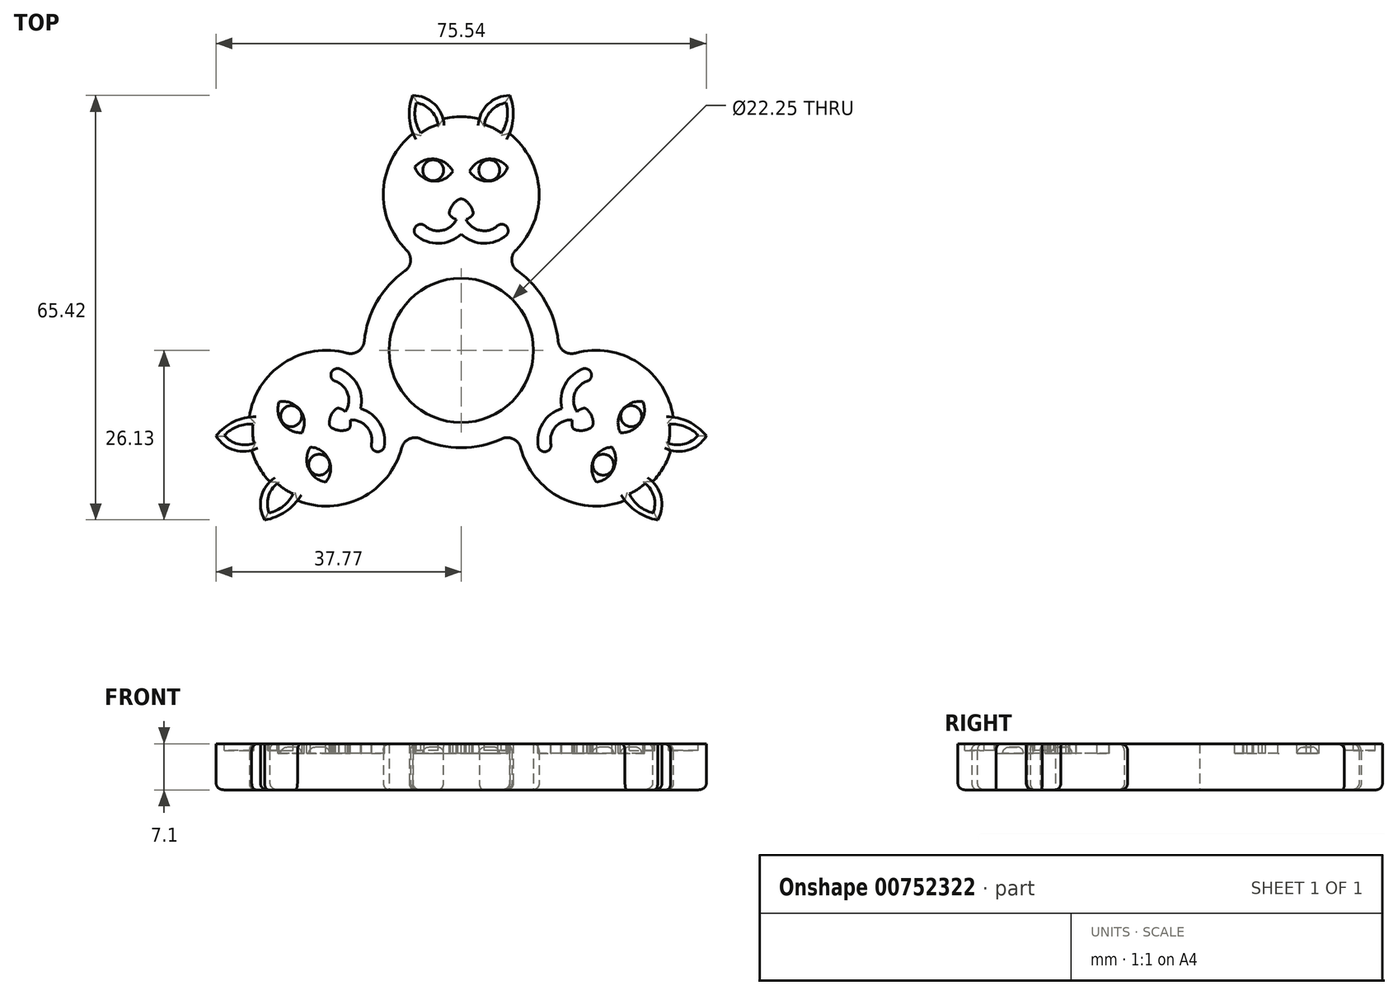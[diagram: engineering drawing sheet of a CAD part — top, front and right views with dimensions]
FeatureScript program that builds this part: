
annotation { "Feature Type Name" : "Feature", "Feature Type Description" : "" }
export const myFeature = defineFeature(function(context is Context, id is Id, definition is map)
    precondition{}
    {
        {
            var Q0;
            Q0=qCreatedBy(makeId("Top.planeOp"),FACE);
            var sketch = newSketch(context, id + "F0", { "sketchPlane" : qUnion([Q0])});
            skCircle(sketch, "E0", {"center": v(0, 0) * mm, "radius": 11.13 * mm});
            skCircle(sketch, "E1", {"center": v(0, 0) * mm, "radius": 15 * mm});
            skSolve(sketch);
        }
        {
            var Q0;
            Q0 = qSketchRegion(id + "F0", true);
            extrude(context, id + "F1", {"entities" : qUnion([Q0]), "depth" : 7.1 * mm, "offsetDistance" : 25 * mm});
        }
        {
            var Q0;
            Q0=qCreatedBy(makeId("Top.planeOp"),FACE);
            var sketch = newSketch(context, id + "F2", { "sketchPlane" : qUnion([Q0])});
            skArc(sketch, "E2", {"start": v(-7.5, 39.3) * mm, "mid": v(-8.02, 36.35) * mm, "end": v(-7.42, 33.43) * mm});
            skArc(sketch, "E3", {"start": v(-2.8, 35.67) * mm, "mid": v(-4.52, 38.28) * mm, "end": v(-7.5, 39.3) * mm});
            skArc(sketch, "E4", {"start": v(-8.69, 12.23) * mm, "mid": v(-7.8, 13.78) * mm, "end": v(-8.43, 15.46) * mm});
            skArc(sketch, "E5.MirrorCS", {"start": v(2.8, 35.67) * mm, "mid": v(4.52, 38.28) * mm, "end": v(7.5, 39.3) * mm});
            skArc(sketch, "E6.MirrorCS", {"start": v(7.5, 39.3) * mm, "mid": v(8.02, 36.35) * mm, "end": v(7.42, 33.43) * mm});
            skArc(sketch, "E7.MirrorCS", {"start": v(8.69, 12.23) * mm, "mid": v(7.8, 13.78) * mm, "end": v(8.43, 15.46) * mm});
            skArc(sketch, "E8", {"start": v(8.43, 15.46) * mm, "mid": v(11.98, 24.67) * mm, "end": v(7.42, 33.43) * mm});
            skArc(sketch, "E9", {"start": v(8.69, 12.23) * mm, "mid": v(0, 15) * mm, "end": v(-8.69, 12.23) * mm});
            skArc(sketch, "E10", {"start": v(2.8, 35.67) * mm, "mid": v(0, 36) * mm, "end": v(-2.8, 35.67) * mm});
            skArc(sketch, "E11", {"start": v(-7.42, 33.43) * mm, "mid": v(-11.98, 24.67) * mm, "end": v(-8.43, 15.46) * mm});
            skArc(sketch, "E12.1.0", {"start": v(-30.28, -26.13) * mm, "mid": v(-27.48, -25.12) * mm, "end": v(-25.24, -23.14) * mm});
            skArc(sketch, "E12.1.1", {"start": v(-32.29, -15.42) * mm, "mid": v(-35.42, -15.22) * mm, "end": v(-37.77, -13.16) * mm});
            skArc(sketch, "E12.1.2", {"start": v(-29.5, -20.25) * mm, "mid": v(-30.9, -23.06) * mm, "end": v(-30.28, -26.13) * mm});
            skArc(sketch, "E12.1.3", {"start": v(-17.6, -0.43) * mm, "mid": v(-27.35, -1.96) * mm, "end": v(-32.66, -10.28) * mm});
            skArc(sketch, "E12.1.4", {"start": v(-14.93, 1.4) * mm, "mid": v(-13, -7.5) * mm, "end": v(-6.25, -13.64) * mm});
            skArc(sketch, "E12.1.5", {"start": v(-37.77, -13.16) * mm, "mid": v(-35.5, -11.23) * mm, "end": v(-32.66, -10.28) * mm});
            skArc(sketch, "E12.1.6", {"start": v(-25.24, -23.14) * mm, "mid": v(-15.37, -22.71) * mm, "end": v(-9.17, -15.03) * mm});
            skArc(sketch, "E12.1.7", {"start": v(-32.29, -15.42) * mm, "mid": v(-31.18, -18) * mm, "end": v(-29.5, -20.25) * mm});
            skArc(sketch, "E12.1.8", {"start": v(-6.25, -13.64) * mm, "mid": v(-8.03, -13.65) * mm, "end": v(-9.17, -15.03) * mm});
            skArc(sketch, "E12.1.9", {"start": v(-14.93, 1.4) * mm, "mid": v(-15.84, -0.13) * mm, "end": v(-17.6, -0.43) * mm});
            skArc(sketch, "E12.2.0", {"start": v(37.77, -13.16) * mm, "mid": v(35.5, -11.23) * mm, "end": v(32.66, -10.28) * mm});
            skArc(sketch, "E12.2.1", {"start": v(29.5, -20.25) * mm, "mid": v(30.9, -23.06) * mm, "end": v(30.28, -26.13) * mm});
            skArc(sketch, "E12.2.2", {"start": v(32.29, -15.42) * mm, "mid": v(35.42, -15.22) * mm, "end": v(37.77, -13.16) * mm});
            skArc(sketch, "E12.2.3", {"start": v(9.17, -15.03) * mm, "mid": v(15.37, -22.71) * mm, "end": v(25.24, -23.14) * mm});
            skArc(sketch, "E12.2.4", {"start": v(6.25, -13.64) * mm, "mid": v(13, -7.5) * mm, "end": v(14.93, 1.4) * mm});
            skArc(sketch, "E12.2.5", {"start": v(30.28, -26.13) * mm, "mid": v(27.48, -25.12) * mm, "end": v(25.24, -23.14) * mm});
            skArc(sketch, "E12.2.6", {"start": v(32.66, -10.28) * mm, "mid": v(27.35, -1.96) * mm, "end": v(17.6, -0.43) * mm});
            skArc(sketch, "E12.2.7", {"start": v(29.5, -20.25) * mm, "mid": v(31.18, -18) * mm, "end": v(32.29, -15.42) * mm});
            skArc(sketch, "E12.2.8", {"start": v(14.93, 1.4) * mm, "mid": v(15.84, -0.13) * mm, "end": v(17.6, -0.43) * mm});
            skArc(sketch, "E12.2.9", {"start": v(6.25, -13.64) * mm, "mid": v(8.03, -13.65) * mm, "end": v(9.17, -15.03) * mm});
            skSolve(sketch);
        }
        {
            var Q0;
            Q0 = qSketchRegion(id + "F2", true);
            extrude(context, id + "F3", {"entities" : qUnion([Q0]), "operationType" : NewBodyOperationType.ADD, "depth" : 7.1 * mm, "offsetDistance" : 25 * mm});
        }
        {
            var Q0;
            Q0=makeQuery(id+"F3.boolean.opBoolean","MERGE",FACE,{"derivedFrom":[makeQuery(id+"F1.opExtrude","CAP_FACE",FACE,{"disambiguationData":[OSD([sQuery(id+"F0.wireOp",EDGE,"E0"),sQuery(id+"F0.wireOp",EDGE,"E1")])],"isStart":false}),makeQuery(id+"F3.opExtrude","CAP_FACE",FACE,{"disambiguationData":[OSD([sQuery(id+"F2.wireOp",EDGE,"E2"),sQuery(id+"F2.wireOp",EDGE,"E3"),sQuery(id+"F2.wireOp",EDGE,"E4"),sQuery(id+"F2.wireOp",EDGE,"E5.MirrorCS"),sQuery(id+"F2.wireOp",EDGE,"E6.MirrorCS"),sQuery(id+"F2.wireOp",EDGE,"E7.MirrorCS"),sQuery(id+"F2.wireOp",EDGE,"E8"),sQuery(id+"F2.wireOp",EDGE,"E9"),sQuery(id+"F2.wireOp",EDGE,"E10"),sQuery(id+"F2.wireOp",EDGE,"E11")])],"isStart":false}),makeQuery(id+"F3.opExtrude","CAP_FACE",FACE,{"disambiguationData":[OSD([sQuery(id+"F2.wireOp",EDGE,"E12.1.0"),sQuery(id+"F2.wireOp",EDGE,"E12.1.1"),sQuery(id+"F2.wireOp",EDGE,"E12.1.2"),sQuery(id+"F2.wireOp",EDGE,"E12.1.3"),sQuery(id+"F2.wireOp",EDGE,"E12.1.4"),sQuery(id+"F2.wireOp",EDGE,"E12.1.5"),sQuery(id+"F2.wireOp",EDGE,"E12.1.6"),sQuery(id+"F2.wireOp",EDGE,"E12.1.7"),sQuery(id+"F2.wireOp",EDGE,"E12.1.8"),sQuery(id+"F2.wireOp",EDGE,"E12.1.9")])],"isStart":false}),makeQuery(id+"F3.opExtrude","CAP_FACE",FACE,{"disambiguationData":[OSD([sQuery(id+"F2.wireOp",EDGE,"E12.2.0"),sQuery(id+"F2.wireOp",EDGE,"E12.2.1"),sQuery(id+"F2.wireOp",EDGE,"E12.2.2"),sQuery(id+"F2.wireOp",EDGE,"E12.2.3"),sQuery(id+"F2.wireOp",EDGE,"E12.2.4"),sQuery(id+"F2.wireOp",EDGE,"E12.2.5"),sQuery(id+"F2.wireOp",EDGE,"E12.2.6"),sQuery(id+"F2.wireOp",EDGE,"E12.2.7"),sQuery(id+"F2.wireOp",EDGE,"E12.2.8"),sQuery(id+"F2.wireOp",EDGE,"E12.2.9")])],"isStart":false})]});
            var sketch = newSketch(context, id + "F4", { "sketchPlane" : qUnion([Q0])});
            skArc(sketch, "E13", {"start": v(-1.28, 27.6) * mm, "mid": v(-4.05, 29.48) * mm, "end": v(-7.16, 28.24) * mm});
            skArc(sketch, "E14", {"start": v(-7.16, 28.24) * mm, "mid": v(-4.42, 26.1) * mm, "end": v(-1.28, 27.6) * mm});
            skArc(sketch, "E15", {"start": v(0, 23.34) * mm, "mid": v(-0.27, 23.3) * mm, "end": v(-0.5, 23.19) * mm});
            skArc(sketch, "E16", {"start": v(-0.5, 23.19) * mm, "mid": v(-1.36, 22.37) * mm, "end": v(-1.83, 21.28) * mm});
            skArc(sketch, "E17", {"start": v(-1.67, 20.75) * mm, "mid": v(-1.24, 20.41) * mm, "end": v(-0.74, 20.18) * mm});
            skArc(sketch, "E18", {"start": v(-1.83, 21.28) * mm, "mid": v(-1.81, 21) * mm, "end": v(-1.67, 20.75) * mm});
            skArc(sketch, "E19.MirrorCS", {"start": v(0, 23.34) * mm, "mid": v(0.27, 23.3) * mm, "end": v(0.5, 23.19) * mm});
            skArc(sketch, "E20.MirrorCS", {"start": v(0.5, 23.19) * mm, "mid": v(1.36, 22.37) * mm, "end": v(1.83, 21.28) * mm});
            skArc(sketch, "E21.MirrorCS", {"start": v(1.83, 21.28) * mm, "mid": v(1.81, 21) * mm, "end": v(1.67, 20.75) * mm});
            skArc(sketch, "E22.MirrorCS", {"start": v(1.67, 20.75) * mm, "mid": v(1.24, 20.41) * mm, "end": v(0.74, 20.18) * mm});
            skArc(sketch, "E23", {"start": v(-5.68, 19.27) * mm, "mid": v(-2.98, 18.47) * mm, "end": v(-0.74, 20.18) * mm});
            skArc(sketch, "E24", {"start": v(-7, 17.76) * mm, "mid": v(-3.47, 16.5) * mm, "end": v(0, 17.9) * mm});
            skArc(sketch, "E25", {"start": v(-5.68, 19.27) * mm, "mid": v(-7, 19.1) * mm, "end": v(-7, 17.76) * mm});
            skArc(sketch, "E26.MirrorCS", {"start": v(5.68, 19.27) * mm, "mid": v(2.98, 18.47) * mm, "end": v(0.74, 20.18) * mm});
            skArc(sketch, "E27.MirrorCS", {"start": v(5.68, 19.27) * mm, "mid": v(7, 19.1) * mm, "end": v(7, 17.76) * mm});
            skArc(sketch, "E28.MirrorCS", {"start": v(7, 17.76) * mm, "mid": v(3.47, 16.5) * mm, "end": v(0, 17.9) * mm});
            skArc(sketch, "E29.MirrorCS", {"start": v(7.16, 28.24) * mm, "mid": v(4.42, 26.1) * mm, "end": v(1.28, 27.6) * mm});
            skArc(sketch, "E30.MirrorCS", {"start": v(1.28, 27.6) * mm, "mid": v(4.05, 29.48) * mm, "end": v(7.16, 28.24) * mm});
            skLineSegment(sketch, "E31", {"start": v(0, 20.06) * mm, "end": v(0, 20.06) * mm});
            skArc(sketch, "E32.1.0", {"start": v(-24.54, -12.68) * mm, "mid": v(-27.55, -11.23) * mm, "end": v(-28.04, -7.92) * mm});
            skArc(sketch, "E32.1.1", {"start": v(-19.53, -4.72) * mm, "mid": v(-17.49, -6.66) * mm, "end": v(-17.85, -9.45) * mm});
            skArc(sketch, "E32.1.2", {"start": v(-18.88, -2.83) * mm, "mid": v(-16.02, -5.24) * mm, "end": v(-15.5, -8.95) * mm});
            skArc(sketch, "E32.1.3", {"start": v(-28.04, -7.92) * mm, "mid": v(-24.8, -9.22) * mm, "end": v(-24.54, -12.68) * mm});
            skArc(sketch, "E32.1.4", {"start": v(-23.25, -14.9) * mm, "mid": v(-23.5, -18.25) * mm, "end": v(-20.88, -20.32) * mm});
            skArc(sketch, "E32.1.5", {"start": v(-13.85, -14.55) * mm, "mid": v(-13.04, -15.6) * mm, "end": v(-11.89, -14.94) * mm});
            skArc(sketch, "E32.1.6", {"start": v(-20.88, -20.32) * mm, "mid": v(-20.38, -16.88) * mm, "end": v(-23.25, -14.9) * mm});
            skArc(sketch, "E32.1.7", {"start": v(-11.89, -14.94) * mm, "mid": v(-12.55, -11.25) * mm, "end": v(-15.5, -8.95) * mm});
            skArc(sketch, "E32.1.8", {"start": v(-13.85, -14.55) * mm, "mid": v(-14.5, -11.82) * mm, "end": v(-17.1, -10.73) * mm});
            skArc(sketch, "E32.1.9", {"start": v(-19.53, -4.72) * mm, "mid": v(-20.03, -3.49) * mm, "end": v(-18.88, -2.83) * mm});
            skArc(sketch, "E32.1.10", {"start": v(-19.35, -9.06) * mm, "mid": v(-19.1, -8.93) * mm, "end": v(-18.8, -8.93) * mm});
            skArc(sketch, "E32.1.11", {"start": v(-18.8, -8.93) * mm, "mid": v(-18.3, -9.13) * mm, "end": v(-17.85, -9.45) * mm});
            skArc(sketch, "E32.1.12", {"start": v(-20.21, -11.67) * mm, "mid": v(-20.05, -11.88) * mm, "end": v(-19.83, -12.03) * mm});
            skArc(sketch, "E32.1.13", {"start": v(-19.83, -12.03) * mm, "mid": v(-18.7, -12.36) * mm, "end": v(-17.52, -12.22) * mm});
            skArc(sketch, "E32.1.14", {"start": v(-20.33, -11.15) * mm, "mid": v(-20.05, -10) * mm, "end": v(-19.35, -9.06) * mm});
            skArc(sketch, "E32.1.15", {"start": v(-17.14, -11.82) * mm, "mid": v(-17.06, -11.28) * mm, "end": v(-17.1, -10.73) * mm});
            skArc(sketch, "E32.1.16", {"start": v(-17.52, -12.22) * mm, "mid": v(-17.28, -12.07) * mm, "end": v(-17.14, -11.82) * mm});
            skArc(sketch, "E32.1.17", {"start": v(-20.21, -11.67) * mm, "mid": v(-20.31, -11.42) * mm, "end": v(-20.33, -11.15) * mm});
            skArc(sketch, "E32.2.0", {"start": v(23.25, -14.9) * mm, "mid": v(23.5, -18.25) * mm, "end": v(20.88, -20.32) * mm});
            skArc(sketch, "E32.2.1", {"start": v(13.85, -14.55) * mm, "mid": v(14.5, -11.82) * mm, "end": v(17.1, -10.73) * mm});
            skArc(sketch, "E32.2.2", {"start": v(11.89, -14.94) * mm, "mid": v(12.55, -11.25) * mm, "end": v(15.5, -8.95) * mm});
            skArc(sketch, "E32.2.3", {"start": v(20.88, -20.32) * mm, "mid": v(20.38, -16.88) * mm, "end": v(23.25, -14.9) * mm});
            skArc(sketch, "E32.2.4", {"start": v(24.54, -12.68) * mm, "mid": v(27.55, -11.23) * mm, "end": v(28.04, -7.92) * mm});
            skArc(sketch, "E32.2.5", {"start": v(19.53, -4.72) * mm, "mid": v(20.03, -3.49) * mm, "end": v(18.88, -2.83) * mm});
            skArc(sketch, "E32.2.6", {"start": v(28.04, -7.92) * mm, "mid": v(24.8, -9.22) * mm, "end": v(24.54, -12.68) * mm});
            skArc(sketch, "E32.2.7", {"start": v(18.88, -2.83) * mm, "mid": v(16.02, -5.24) * mm, "end": v(15.5, -8.95) * mm});
            skArc(sketch, "E32.2.8", {"start": v(19.53, -4.72) * mm, "mid": v(17.49, -6.66) * mm, "end": v(17.85, -9.45) * mm});
            skArc(sketch, "E32.2.9", {"start": v(13.85, -14.55) * mm, "mid": v(13.04, -15.6) * mm, "end": v(11.89, -14.94) * mm});
            skArc(sketch, "E32.2.10", {"start": v(17.52, -12.22) * mm, "mid": v(17.28, -12.07) * mm, "end": v(17.14, -11.82) * mm});
            skArc(sketch, "E32.2.11", {"start": v(17.14, -11.82) * mm, "mid": v(17.06, -11.28) * mm, "end": v(17.1, -10.73) * mm});
            skArc(sketch, "E32.2.12", {"start": v(20.21, -11.67) * mm, "mid": v(20.31, -11.42) * mm, "end": v(20.33, -11.15) * mm});
            skArc(sketch, "E32.2.13", {"start": v(20.33, -11.15) * mm, "mid": v(20.05, -10) * mm, "end": v(19.35, -9.06) * mm});
            skArc(sketch, "E32.2.14", {"start": v(19.83, -12.03) * mm, "mid": v(18.7, -12.36) * mm, "end": v(17.52, -12.22) * mm});
            skArc(sketch, "E32.2.15", {"start": v(18.8, -8.93) * mm, "mid": v(18.3, -9.13) * mm, "end": v(17.85, -9.45) * mm});
            skArc(sketch, "E32.2.16", {"start": v(19.35, -9.06) * mm, "mid": v(19.1, -8.93) * mm, "end": v(18.8, -8.93) * mm});
            skArc(sketch, "E32.2.17", {"start": v(20.21, -11.67) * mm, "mid": v(20.05, -11.88) * mm, "end": v(19.83, -12.03) * mm});
            skPoint(sketch, "E32.center", {"position": v(0, 0) * mm});
            skSolve(sketch);
        }
        {
            var Q0;
            Q0 = qSketchRegion(id + "F4", true);
            extrude(context, id + "F5", {"entities" : qUnion([Q0]), "operationType" : NewBodyOperationType.REMOVE, "oppositeDirection" : true, "depth" : 1.5 * mm, "offsetDistance" : 25 * mm});
        }
        {
            var Q0;
            Q0=makeQuery(id+"F5.boolean.opBoolean","COPY",FACE,{"derivedFrom":makeQuery(id+"F5.opExtrude","CAP_FACE",FACE,{"disambiguationData":[OSD([sQuery(id+"F4.wireOp",EDGE,"E13"),sQuery(id+"F4.wireOp",EDGE,"E14")])],"isStart":false})});
            var sketch = newSketch(context, id + "F6", { "sketchPlane" : qUnion([Q0])});
            skCircle(sketch, "E33", {"center": v(-4.32, 27.76) * mm, "radius": 1.61 * mm});
            skCircle(sketch, "E34.MirrorC", {"center": v(4.32, 27.76) * mm, "radius": 1.61 * mm});
            skCircle(sketch, "E35.1.0", {"center": v(-21.88, -17.62) * mm, "radius": 1.61 * mm});
            skCircle(sketch, "E35.1.1", {"center": v(-26.2, -10.14) * mm, "radius": 1.61 * mm});
            skCircle(sketch, "E35.2.0", {"center": v(26.2, -10.14) * mm, "radius": 1.61 * mm});
            skCircle(sketch, "E35.2.1", {"center": v(21.88, -17.62) * mm, "radius": 1.61 * mm});
            skPoint(sketch, "E35.center", {"position": v(0, 0) * mm});
            skSolve(sketch);
        }
        {
            var Q0;
            Q0 = qSketchRegion(id + "F6", true);
            extrude(context, id + "F7", {"entities" : qUnion([Q0]), "operationType" : NewBodyOperationType.ADD, "depth" : 1 * mm, "offsetDistance" : 25 * mm});
        }
        {
            var Q0;
            Q0=makeQuery(id+"F7.opExtrude","CAP_FACE",FACE,{"disambiguationData":[OSD([sQuery(id+"F6.wireOp",EDGE,"E34.MirrorC")])],"isStart":false});
            var Q1;
            Q1=makeQuery(id+"F7.opExtrude","CAP_FACE",FACE,{"disambiguationData":[OSD([sQuery(id+"F6.wireOp",EDGE,"E33")])],"isStart":false});
            var Q2;
            Q2=makeQuery(id+"F7.opExtrude","CAP_FACE",FACE,{"disambiguationData":[OSD([sQuery(id+"F6.wireOp",EDGE,"E35.1.1")])],"isStart":false});
            var Q3;
            Q3=makeQuery(id+"F7.opExtrude","CAP_FACE",FACE,{"disambiguationData":[OSD([sQuery(id+"F6.wireOp",EDGE,"E35.1.0")])],"isStart":false});
            var Q4;
            Q4=makeQuery(id+"F7.opExtrude","CAP_FACE",FACE,{"disambiguationData":[OSD([sQuery(id+"F6.wireOp",EDGE,"E35.2.1")])],"isStart":false});
            var Q5;
            Q5=makeQuery(id+"F7.opExtrude","CAP_FACE",FACE,{"disambiguationData":[OSD([sQuery(id+"F6.wireOp",EDGE,"E35.2.0")])],"isStart":false});
            fillet(context, id + "F8", {"entities" : qUnion([Q0, Q1, Q2, Q3, Q4, Q5]), "radius" : 1 * mm, "tangentPropagation" : true, "allowEdgeOverflow" : false});
        }
        {
            var Q0;
            Q0=makeQuery(id+"F3.boolean.opBoolean","MERGE",FACE,{"derivedFrom":[makeQuery(id+"F1.opExtrude","CAP_FACE",FACE,{"disambiguationData":[OSD([sQuery(id+"F0.wireOp",EDGE,"E0"),sQuery(id+"F0.wireOp",EDGE,"E1")])],"isStart":false}),makeQuery(id+"F3.opExtrude","CAP_FACE",FACE,{"disambiguationData":[OSD([sQuery(id+"F2.wireOp",EDGE,"E2"),sQuery(id+"F2.wireOp",EDGE,"E3"),sQuery(id+"F2.wireOp",EDGE,"E4"),sQuery(id+"F2.wireOp",EDGE,"E5.MirrorCS"),sQuery(id+"F2.wireOp",EDGE,"E6.MirrorCS"),sQuery(id+"F2.wireOp",EDGE,"E7.MirrorCS"),sQuery(id+"F2.wireOp",EDGE,"E8"),sQuery(id+"F2.wireOp",EDGE,"E9"),sQuery(id+"F2.wireOp",EDGE,"E10"),sQuery(id+"F2.wireOp",EDGE,"E11")])],"isStart":false}),makeQuery(id+"F3.opExtrude","CAP_FACE",FACE,{"disambiguationData":[OSD([sQuery(id+"F2.wireOp",EDGE,"E12.1.0"),sQuery(id+"F2.wireOp",EDGE,"E12.1.1"),sQuery(id+"F2.wireOp",EDGE,"E12.1.2"),sQuery(id+"F2.wireOp",EDGE,"E12.1.3"),sQuery(id+"F2.wireOp",EDGE,"E12.1.4"),sQuery(id+"F2.wireOp",EDGE,"E12.1.5"),sQuery(id+"F2.wireOp",EDGE,"E12.1.6"),sQuery(id+"F2.wireOp",EDGE,"E12.1.7"),sQuery(id+"F2.wireOp",EDGE,"E12.1.8"),sQuery(id+"F2.wireOp",EDGE,"E12.1.9")])],"isStart":false}),makeQuery(id+"F3.opExtrude","CAP_FACE",FACE,{"disambiguationData":[OSD([sQuery(id+"F2.wireOp",EDGE,"E12.2.0"),sQuery(id+"F2.wireOp",EDGE,"E12.2.1"),sQuery(id+"F2.wireOp",EDGE,"E12.2.2"),sQuery(id+"F2.wireOp",EDGE,"E12.2.3"),sQuery(id+"F2.wireOp",EDGE,"E12.2.4"),sQuery(id+"F2.wireOp",EDGE,"E12.2.5"),sQuery(id+"F2.wireOp",EDGE,"E12.2.6"),sQuery(id+"F2.wireOp",EDGE,"E12.2.7"),sQuery(id+"F2.wireOp",EDGE,"E12.2.8"),sQuery(id+"F2.wireOp",EDGE,"E12.2.9")])],"isStart":false})]});
            var sketch = newSketch(context, id + "F9", { "sketchPlane" : qUnion([Q0])});
            skArc(sketch, "E36", {"start": v(-6.91, 38.15) * mm, "mid": v(-7.08, 35.73) * mm, "end": v(-6.2, 33.46) * mm});
            skArc(sketch, "E37", {"start": v(-3.56, 34.8) * mm, "mid": v(-4.7, 37.02) * mm, "end": v(-6.91, 38.15) * mm});
            skArc(sketch, "E38.MirrorCS", {"start": v(3.56, 34.8) * mm, "mid": v(4.7, 37.02) * mm, "end": v(6.91, 38.15) * mm});
            skArc(sketch, "E39.MirrorCS", {"start": v(6.91, 38.15) * mm, "mid": v(7.08, 35.73) * mm, "end": v(6.2, 33.46) * mm});
            skArc(sketch, "E40.1.1", {"start": v(-36.5, -13.1) * mm, "mid": v(-34.48, -11.73) * mm, "end": v(-32.08, -11.37) * mm});
            skArc(sketch, "E40.1.2", {"start": v(-31.92, -14.31) * mm, "mid": v(-34.4, -14.44) * mm, "end": v(-36.5, -13.1) * mm});
            skArc(sketch, "E40.1.4", {"start": v(-28.36, -20.49) * mm, "mid": v(-29.7, -22.58) * mm, "end": v(-29.59, -25.06) * mm});
            skArc(sketch, "E40.1.5", {"start": v(-29.59, -25.06) * mm, "mid": v(-27.4, -24) * mm, "end": v(-25.88, -22.1) * mm});
            skArc(sketch, "E40.2.1", {"start": v(29.59, -25.06) * mm, "mid": v(27.4, -24) * mm, "end": v(25.88, -22.1) * mm});
            skArc(sketch, "E40.2.2", {"start": v(28.36, -20.49) * mm, "mid": v(29.7, -22.58) * mm, "end": v(29.59, -25.06) * mm});
            skArc(sketch, "E40.2.4", {"start": v(31.92, -14.31) * mm, "mid": v(34.4, -14.44) * mm, "end": v(36.5, -13.1) * mm});
            skArc(sketch, "E40.2.5", {"start": v(36.5, -13.1) * mm, "mid": v(34.48, -11.73) * mm, "end": v(32.08, -11.37) * mm});
            skPoint(sketch, "E40.center", {"position": v(0, 0) * mm});
            skArc(sketch, "E41", {"start": v(-3.56, 34.8) * mm, "mid": v(-4.94, 34.26) * mm, "end": v(-6.2, 33.46) * mm});
            skPoint(sketch, "E42.orphan", {"position": v(-3.71, 35.41) * mm});
            skPoint(sketch, "E43.orphan", {"position": v(-6.54, 34.06) * mm});
            skArc(sketch, "E44.MirrorCS", {"start": v(3.56, 34.8) * mm, "mid": v(4.94, 34.26) * mm, "end": v(6.2, 33.46) * mm});
            skArc(sketch, "E45.1.0", {"start": v(-28.36, -20.49) * mm, "mid": v(-27.2, -21.41) * mm, "end": v(-25.88, -22.1) * mm});
            skArc(sketch, "E45.1.1", {"start": v(-31.92, -14.31) * mm, "mid": v(-32.14, -12.85) * mm, "end": v(-32.08, -11.37) * mm});
            skArc(sketch, "E45.2.0", {"start": v(31.92, -14.31) * mm, "mid": v(32.14, -12.85) * mm, "end": v(32.08, -11.37) * mm});
            skArc(sketch, "E45.2.1", {"start": v(28.36, -20.49) * mm, "mid": v(27.2, -21.41) * mm, "end": v(25.88, -22.1) * mm});
            skPoint(sketch, "E46.orphan", {"position": v(3.71, 35.41) * mm});
            skPoint(sketch, "E47.orphan", {"position": v(6.54, 34.06) * mm});
            skPoint(sketch, "E48.orphan", {"position": v(-32.77, -11.36) * mm});
            skPoint(sketch, "E49.orphan", {"position": v(-32.52, -14.5) * mm});
            skPoint(sketch, "E50.orphan", {"position": v(-28.81, -20.92) * mm});
            skPoint(sketch, "E51.orphan", {"position": v(-26.22, -22.7) * mm});
            skPoint(sketch, "E52.orphan", {"position": v(32.77, -11.36) * mm});
            skPoint(sketch, "E53.orphan", {"position": v(32.52, -14.5) * mm});
            skPoint(sketch, "E54.orphan", {"position": v(28.81, -20.92) * mm});
            skPoint(sketch, "E55.orphan", {"position": v(26.22, -22.7) * mm});
            skSolve(sketch);
        }
        {
            var Q0;
            Q0 = qSketchRegion(id + "F9", true);
            extrude(context, id + "F10", {"entities" : qUnion([Q0]), "operationType" : NewBodyOperationType.REMOVE, "oppositeDirection" : true, "depth" : 1 * mm, "offsetDistance" : 25 * mm});
        }
        {
            var Q0;
            Q0=makeQuery(id+"F3.opExtrude","CAP_EDGE",EDGE,{"disambiguationData":[OSD([sQuery(id+"F2.wireOp",EDGE,"E11")])],"isStart":false});
            var Q1;
            Q1=makeQuery(id+"F3.opExtrude","CAP_EDGE",EDGE,{"disambiguationData":[OSD([sQuery(id+"F2.wireOp",EDGE,"E10")])],"isStart":false});
            var Q2;
            Q2=makeQuery(id+"F3.opExtrude","CAP_EDGE",EDGE,{"disambiguationData":[OSD([sQuery(id+"F2.wireOp",EDGE,"E8")])],"isStart":false});
            var Q3;
            Q3=makeQuery(id+"F3.opExtrude","CAP_EDGE",EDGE,{"disambiguationData":[OSD([sQuery(id+"F2.wireOp",EDGE,"E12.2.7")])],"isStart":false});
            var Q4;
            Q4=makeQuery(id+"F3.opExtrude","CAP_EDGE",EDGE,{"disambiguationData":[OSD([sQuery(id+"F2.wireOp",EDGE,"E12.2.3")])],"isStart":false});
            var Q5;
            Q5=makeQuery(id+"F3.opExtrude","CAP_EDGE",EDGE,{"disambiguationData":[OSD([sQuery(id+"F2.wireOp",EDGE,"E12.1.7")])],"isStart":false});
            fillet(context, id + "F11", {"entities" : qUnion([Q0, Q1, Q2, Q3, Q4, Q5]), "radius" : 1 * mm, "tangentPropagation" : true, "allowEdgeOverflow" : false});
        }
        {
            var Q0;
            Q0=makeQuery(id+"F3.opExtrude","CAP_EDGE",EDGE,{"disambiguationData":[OSD([sQuery(id+"F2.wireOp",EDGE,"E12.2.6")])],"isStart":true});
            var Q1;
            Q1=makeQuery(id+"F3.opExtrude","CAP_EDGE",EDGE,{"disambiguationData":[OSD([sQuery(id+"F2.wireOp",EDGE,"E6.MirrorCS")])],"isStart":true});
            var Q2;
            Q2=makeQuery(id+"F3.opExtrude","CAP_EDGE",EDGE,{"disambiguationData":[OSD([sQuery(id+"F2.wireOp",EDGE,"E5.MirrorCS")])],"isStart":true});
            var Q3;
            Q3=makeQuery(id+"F3.opExtrude","CAP_EDGE",EDGE,{"disambiguationData":[OSD([sQuery(id+"F2.wireOp",EDGE,"E10")])],"isStart":true});
            var Q4;
            Q4=makeQuery(id+"F3.opExtrude","CAP_EDGE",EDGE,{"disambiguationData":[OSD([sQuery(id+"F2.wireOp",EDGE,"E3")])],"isStart":true});
            var Q5;
            Q5=makeQuery(id+"F3.opExtrude","CAP_EDGE",EDGE,{"disambiguationData":[OSD([sQuery(id+"F2.wireOp",EDGE,"E2")])],"isStart":true});
            var Q6;
            Q6=makeQuery(id+"F3.opExtrude","CAP_EDGE",EDGE,{"disambiguationData":[OSD([sQuery(id+"F2.wireOp",EDGE,"E11")])],"isStart":true});
            var Q7;
            Q7=makeQuery(id+"F3.opExtrude","CAP_EDGE",EDGE,{"disambiguationData":[OSD([sQuery(id+"F2.wireOp",EDGE,"E12.1.5")])],"isStart":true});
            var Q8;
            Q8=makeQuery(id+"F3.opExtrude","CAP_EDGE",EDGE,{"disambiguationData":[OSD([sQuery(id+"F2.wireOp",EDGE,"E12.1.1")])],"isStart":true});
            var Q9;
            Q9=makeQuery(id+"F3.opExtrude","CAP_EDGE",EDGE,{"disambiguationData":[OSD([sQuery(id+"F2.wireOp",EDGE,"E12.1.7")])],"isStart":true});
            var Q10;
            Q10=makeQuery(id+"F3.opExtrude","CAP_EDGE",EDGE,{"disambiguationData":[OSD([sQuery(id+"F2.wireOp",EDGE,"E12.1.2")])],"isStart":true});
            var Q11;
            Q11=makeQuery(id+"F3.opExtrude","CAP_EDGE",EDGE,{"disambiguationData":[OSD([sQuery(id+"F2.wireOp",EDGE,"E12.1.0")])],"isStart":true});
            var Q12;
            Q12=makeQuery(id+"F3.opExtrude","CAP_EDGE",EDGE,{"disambiguationData":[OSD([sQuery(id+"F2.wireOp",EDGE,"E12.1.6")])],"isStart":true});
            var Q13;
            Q13=makeQuery(id+"F3.opExtrude","CAP_EDGE",EDGE,{"disambiguationData":[OSD([sQuery(id+"F2.wireOp",EDGE,"E12.2.5")])],"isStart":true});
            var Q14;
            Q14=makeQuery(id+"F3.opExtrude","CAP_EDGE",EDGE,{"disambiguationData":[OSD([sQuery(id+"F2.wireOp",EDGE,"E12.2.1")])],"isStart":true});
            var Q15;
            Q15=makeQuery(id+"F3.opExtrude","CAP_EDGE",EDGE,{"disambiguationData":[OSD([sQuery(id+"F2.wireOp",EDGE,"E12.2.7")])],"isStart":true});
            var Q16;
            Q16=makeQuery(id+"F3.opExtrude","CAP_EDGE",EDGE,{"disambiguationData":[OSD([sQuery(id+"F2.wireOp",EDGE,"E12.2.2")])],"isStart":true});
            var Q17;
            Q17=makeQuery(id+"F3.opExtrude","CAP_EDGE",EDGE,{"disambiguationData":[OSD([sQuery(id+"F2.wireOp",EDGE,"E12.2.0")])],"isStart":true});
            fillet(context, id + "F12", {"entities" : qUnion([Q0, Q1, Q2, Q3, Q4, Q5, Q6, Q7, Q8, Q9, Q10, Q11, Q12, Q13, Q14, Q15, Q16, Q17]), "radius" : 1 * mm, "tangentPropagation" : true, "allowEdgeOverflow" : false});
        }
    });
